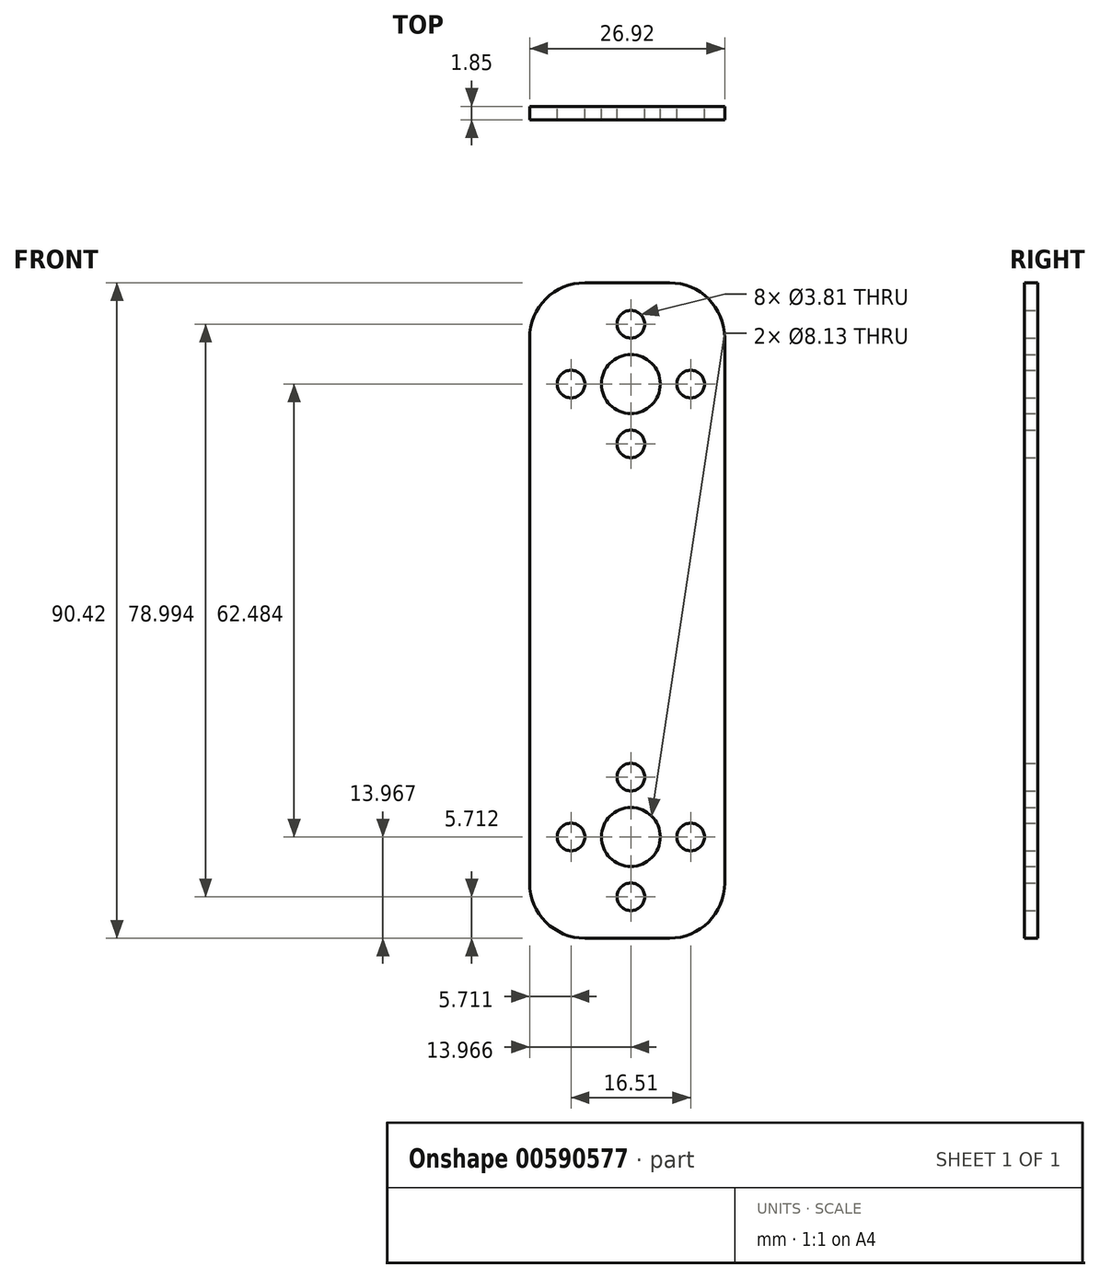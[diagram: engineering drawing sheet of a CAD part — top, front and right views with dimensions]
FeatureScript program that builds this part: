
annotation { "Feature Type Name" : "Feature", "Feature Type Description" : "" }
export const myFeature = defineFeature(function(context is Context, id is Id, definition is map)
    precondition{}
    {
        {
            var Q0;
            Q0=qCreatedBy(makeId("Front.planeOp"),FACE);
            var sketch = newSketch(context, id + "F0", { "sketchPlane" : qUnion([Q0])});
            skLineSegment(sketch, "E0.bottom", {"start": v(-7.62, 41.1) * mm, "end": v(-19.3, 41.1) * mm});
            skLineSegment(sketch, "E0.top", {"start": v(-7.62, -49.33) * mm, "end": v(-19.3, -49.33) * mm});
            skLineSegment(sketch, "E0.left", {"start": v(0, 33.47) * mm, "end": v(0, -41.71) * mm});
            skLineSegment(sketch, "E0.right", {"start": v(-26.92, 33.47) * mm, "end": v(-26.92, -41.71) * mm});
            skPoint(sketch, "E1.visualSharp", {"position": v(-26.92, 41.1) * mm});
            skArc(sketch, "E1.filletArc", {"start": v(-19.3, 41.1) * mm, "mid": v(-24.7, 38.86) * mm, "end": v(-26.92, 33.47) * mm});
            skPoint(sketch, "E2.visualSharp", {"position": v(0, 41.1) * mm});
            skArc(sketch, "E2.filletArc", {"start": v(0, 33.47) * mm, "mid": v(-2.23, 38.86) * mm, "end": v(-7.62, 41.1) * mm});
            skPoint(sketch, "E3.visualSharp", {"position": v(-26.92, -49.33) * mm});
            skArc(sketch, "E3.filletArc", {"start": v(-26.92, -41.71) * mm, "mid": v(-24.7, -47.1) * mm, "end": v(-19.3, -49.33) * mm});
            skPoint(sketch, "E4.visualSharp", {"position": v(0, -49.33) * mm});
            skArc(sketch, "E4.filletArc", {"start": v(-7.62, -49.33) * mm, "mid": v(-2.23, -47.1) * mm, "end": v(0, -41.71) * mm});
            skCircle(sketch, "E5", {"center": v(-12.95, 35.38) * mm, "radius": 1.9 * mm});
            skCircle(sketch, "E6", {"center": v(-12.95, 27.12) * mm, "radius": 4.06 * mm});
            skCircle(sketch, "E7", {"center": v(-21.2, 27.12) * mm, "radius": 1.9 * mm});
            skCircle(sketch, "E8", {"center": v(-12.95, 18.87) * mm, "radius": 1.9 * mm});
            skCircle(sketch, "E9", {"center": v(-4.7, 27.12) * mm, "radius": 1.9 * mm});
            skCircle(sketch, "E10", {"center": v(-12.95, -27.1) * mm, "radius": 1.9 * mm});
            skCircle(sketch, "E11", {"center": v(-12.95, -35.36) * mm, "radius": 4.06 * mm});
            skCircle(sketch, "E12", {"center": v(-21.2, -35.36) * mm, "radius": 1.9 * mm});
            skCircle(sketch, "E13", {"center": v(-12.95, -43.62) * mm, "radius": 1.9 * mm});
            skCircle(sketch, "E14", {"center": v(-4.7, -35.36) * mm, "radius": 1.9 * mm});
            skSolve(sketch);
        }
        {
            var Q0;
            Q0=makeQuery(id+"F0.imprint","IMPRINT",FACE,{"disambiguationData":[TD([[makeQuery(id+"F0.imprint","IMPRINT",EDGE,{"derivedFrom":sQuery(id+"F0.wireOp",EDGE,"E0.bottom")}),1.0]])]});
            extrude(context, id + "F1", {"entities" : qUnion([Q0]), "depth" : 1.85 * mm, "offsetDistance" : 25.4 * mm});
        }
    });
